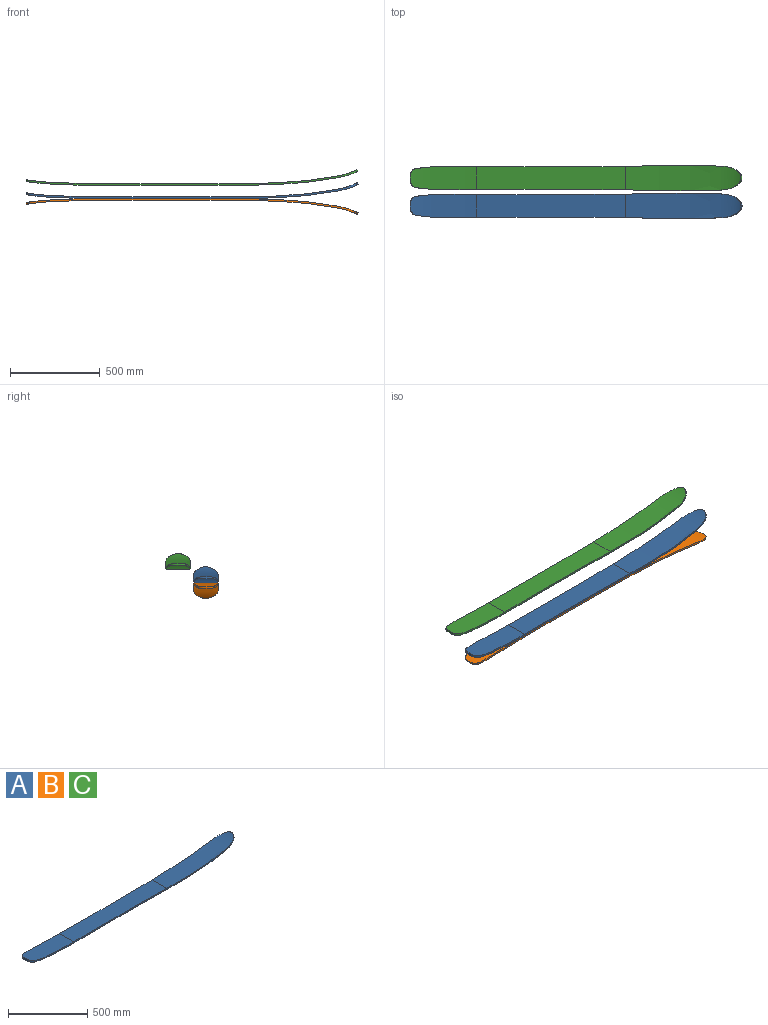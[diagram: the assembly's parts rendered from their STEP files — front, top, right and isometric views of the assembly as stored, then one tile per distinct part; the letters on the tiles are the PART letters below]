
ASSEMBLY  parts=3 mates=1
PART A: 22 faces, bbox 1850x141x88.4 mm
  f0: bspline ~81.59x18.24mm, area 815.7mm2, adj f1,f15,f16,f19
  f1: bspline ~39.22x33.52mm, area 550.4mm2, adj f0,f2,f16,f19
  f2: plane 26.85x9.82mm, normal (-0.98,0,0.19), area 268.5mm2, adj f1,f3,f16,f19
  f3: bspline ~39.22x33.52mm, area 550.4mm2, adj f2,f4,f16,f19
  f4: bspline ~81.59x18.24mm, area 815.7mm2, adj f3,f5,f16,f19
  f5: bspline ~194.23x18.24mm, area 1940.1mm2, adj f4,f6,f16,f19
  f6: bspline ~62.96x10.47mm, area 628.9mm2, adj f5,f7,f16,f19
  f7: cylinder r=31579.76mm len=830mm, axis (0,0,1), area 8300.3mm2, adj f6,f8,f17,f20
  f8: bspline ~191.1x14.35mm, area 1909.6mm2, adj f7,f9,f18,f21
  f9: bspline ~342.88x46.93mm, area 3440.1mm2, adj f8,f10,f18,f21
  f10: bspline ~133.42x118.52mm, area 2990.3mm2, adj f9,f11,f18,f21
  f11: bspline ~342.88x46.93mm, area 3440.1mm2, adj f10,f12,f18,f21
  f12: bspline ~191.1x14.35mm, area 1909.6mm2, adj f11,f13,f18,f21
  f13: cylinder r=31579.76mm len=830mm, axis (0,0,1), area 8300.3mm2, adj f12,f14,f17,f20
  f14: bspline ~62.96x10.47mm, area 628.9mm2, adj f13,f15,f16,f19
  f15: bspline ~194.23x18.24mm, area 1940.1mm2, adj f0,f14,f16,f19
  f16: extruded ~368.09x130mm, area 44986.6mm2, adj f0,f1,f2,f3,f4,f5,f6,f14
  f17: plane 830x131.31mm, normal (0,0,1), area 104541.7mm2, adj f7,f13,f16,f18
  f18: extruded ~644.57x141mm, area 85431.8mm2, adj f8,f9,f10,f11,f12,f17
  f19: extruded ~370x129.39mm, area 44856.6mm2, adj f0,f1,f2,f3,f4,f5,f6,f14
  f20: plane 830x131.31mm, normal (0,0,-1), area 104541.7mm2, adj f7,f13,f19,f21
  f21: extruded ~650x141mm, area 86266.7mm2, adj f8,f9,f10,f11,f12,f20
PART B: same geometry as A
PART C: same geometry as A
PLACE A t=(-199.4,-403.63,164.84)mm
PLACE B rot(axis=(1,0,0),180deg) t=(-199.4,-403.63,-15.16)mm
PLACE C t=(-199.99,-248.69,238.45)mm
MATE fastened B.f20 <-> A.f20  axis (0,0,1) through (-932.51,-403.63,74.84)mm
